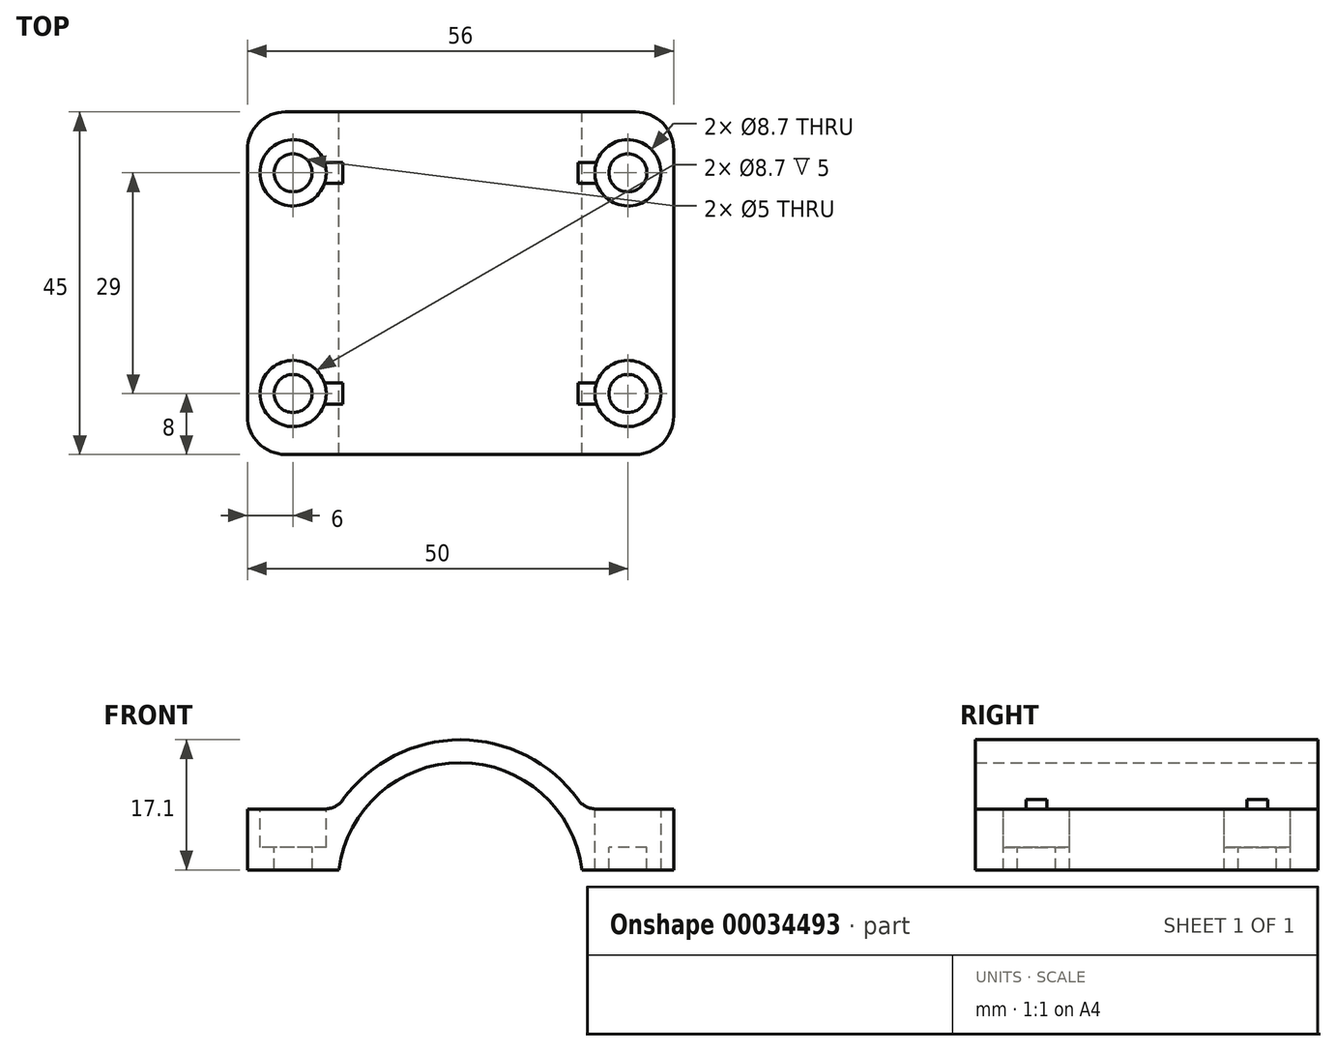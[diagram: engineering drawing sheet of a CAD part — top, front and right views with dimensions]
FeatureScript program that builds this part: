
annotation { "Feature Type Name" : "Feature", "Feature Type Description" : "" }
export const myFeature = defineFeature(function(context is Context, id is Id, definition is map)
    precondition{}
    {
        {
            var Q0;
            Q0=qCreatedBy(makeId("Front.planeOp"),FACE);
            var sketch = newSketch(context, id + "F0", { "sketchPlane" : qUnion([Q0])});
            skCircle(sketch, "E0", {"center": v(0, 0) * mm, "radius": 16.1 * mm, "construction": true});
            skLineSegment(sketch, "E1", {"start": v(-59.3, 0) * mm, "end": v(64.9, 0) * mm, "construction": true});
            skLineSegment(sketch, "E2", {"start": v(-28, 2) * mm, "end": v(-15.98, 2) * mm});
            skArc(sketch, "E3", {"start": v(15.98, 2) * mm, "mid": v(0, 16.1) * mm, "end": v(-15.98, 2) * mm});
            skArc(sketch, "E4.0", {"start": v(16.27, 10) * mm, "mid": v(0, 19.1) * mm, "end": v(-16.27, 10) * mm});
            skLineSegment(sketch, "E5", {"start": v(-28, 2) * mm, "end": v(-28, 10) * mm});
            skLineSegment(sketch, "E6", {"start": v(-28, 10) * mm, "end": v(-16.27, 10) * mm});
            skLineSegment(sketch, "E7", {"start": v(28, 10) * mm, "end": v(28, 2) * mm});
            skLineSegment(sketch, "E8.trimOffspring", {"start": v(16.27, 10) * mm, "end": v(28, 10) * mm});
            skLineSegment(sketch, "E9.trimOffspring", {"start": v(15.98, 2) * mm, "end": v(28, 2) * mm});
            skSolve(sketch);
        }
        {
            var Q0;
            Q0 = qSketchRegion(id + "F0", true);
            extrude(context, id + "F1", {"entities" : qUnion([Q0]), "depth" : 45 * mm});
        }
        {
            var Q0;
            Q0=makeQuery(id+"F1.opExtrude","SWEPT_FACE",FACE,{"disambiguationData":[OSD([sQuery(id+"F0.wireOp",EDGE,"E6")])]});
            var sketch = newSketch(context, id + "F2", { "sketchPlane" : qUnion([Q0])});
            skLineSegment(sketch, "E10", {"start": v(0, 3.28) * mm, "end": v(0, -44.43) * mm, "construction": true});
            skLineSegment(sketch, "E11", {"start": v(-22, 4.04) * mm, "end": v(-22, -45.83) * mm, "construction": true});
            skLineSegment(sketch, "E12.0", {"start": v(-28, -45) * mm, "end": v(-28, 0) * mm, "construction": true});
            skLineSegment(sketch, "E12.1", {"start": v(-28, 0) * mm, "end": v(-16.27, 0) * mm, "construction": true});
            skLineSegment(sketch, "E12.2", {"start": v(-28, -45) * mm, "end": v(-16.27, -45) * mm, "construction": true});
            skCircle(sketch, "E13", {"center": v(-22, -8) * mm, "radius": 4.35 * mm});
            skCircle(sketch, "E14", {"center": v(-22, -37) * mm, "radius": 4.35 * mm});
            skCircle(sketch, "E15", {"center": v(-22, -8) * mm, "radius": 2.5 * mm});
            skCircle(sketch, "E16", {"center": v(-22, -37) * mm, "radius": 2.5 * mm});
            skCircle(sketch, "E17.MirrorC", {"center": v(22, -8) * mm, "radius": 2.5 * mm});
            skCircle(sketch, "E18.MirrorC", {"center": v(22, -8) * mm, "radius": 4.35 * mm});
            skCircle(sketch, "E19.MirrorC", {"center": v(22, -37) * mm, "radius": 2.5 * mm});
            skCircle(sketch, "E20.MirrorC", {"center": v(22, -37) * mm, "radius": 4.35 * mm});
            skSolve(sketch);
        }
        {
            var Q0;
            Q0=makeQuery(id+"F2.imprint","IMPRINT",FACE,{"disambiguationData":[TD([[makeQuery(id+"F2.imprint","IMPRINT",EDGE,{"derivedFrom":sQuery(id+"F2.wireOp",EDGE,"E15")}),1.0]])]});
            var Q1;
            Q1=makeQuery(id+"F2.imprint","IMPRINT",FACE,{"disambiguationData":[TD([[makeQuery(id+"F2.imprint","IMPRINT",EDGE,{"derivedFrom":sQuery(id+"F2.wireOp",EDGE,"E15")}),-1.0]])]});
            var Q2;
            Q2=makeQuery(id+"F2.imprint","IMPRINT",FACE,{"disambiguationData":[TD([[makeQuery(id+"F2.imprint","IMPRINT",EDGE,{"derivedFrom":sQuery(id+"F2.wireOp",EDGE,"E17.MirrorC")}),-1.0]])]});
            var Q3;
            Q3=makeQuery(id+"F2.imprint","IMPRINT",FACE,{"disambiguationData":[TD([[makeQuery(id+"F2.imprint","IMPRINT",EDGE,{"derivedFrom":sQuery(id+"F2.wireOp",EDGE,"E17.MirrorC")}),1.0]])]});
            var Q4;
            Q4=makeQuery(id+"F2.imprint","IMPRINT",FACE,{"disambiguationData":[TD([[makeQuery(id+"F2.imprint","IMPRINT",EDGE,{"derivedFrom":sQuery(id+"F2.wireOp",EDGE,"E19.MirrorC")}),-1.0]])]});
            var Q5;
            Q5=makeQuery(id+"F2.imprint","IMPRINT",FACE,{"disambiguationData":[TD([[makeQuery(id+"F2.imprint","IMPRINT",EDGE,{"derivedFrom":sQuery(id+"F2.wireOp",EDGE,"E19.MirrorC")}),1.0]])]});
            var Q6;
            Q6=makeQuery(id+"F2.imprint","IMPRINT",FACE,{"disambiguationData":[TD([[makeQuery(id+"F2.imprint","IMPRINT",EDGE,{"derivedFrom":sQuery(id+"F2.wireOp",EDGE,"E16")}),1.0]])]});
            var Q7;
            Q7=makeQuery(id+"F2.imprint","IMPRINT",FACE,{"disambiguationData":[TD([[makeQuery(id+"F2.imprint","IMPRINT",EDGE,{"derivedFrom":sQuery(id+"F2.wireOp",EDGE,"E16")}),-1.0]])]});
            extrude(context, id + "F3", {"entities" : qUnion([Q0, Q1, Q2, Q3, Q4, Q5, Q6, Q7]), "operationType" : NewBodyOperationType.REMOVE, "oppositeDirection" : true, "depth" : 5 * mm});
        }
        {
            var Q0;
            Q0=makeQuery(id+"F2.imprint","IMPRINT",FACE,{"disambiguationData":[TD([[makeQuery(id+"F2.imprint","IMPRINT",EDGE,{"derivedFrom":sQuery(id+"F2.wireOp",EDGE,"E15")}),1.0]])]});
            var Q1;
            Q1=makeQuery(id+"F2.imprint","IMPRINT",FACE,{"disambiguationData":[TD([[makeQuery(id+"F2.imprint","IMPRINT",EDGE,{"derivedFrom":sQuery(id+"F2.wireOp",EDGE,"E17.MirrorC")}),-1.0]])]});
            var Q2;
            Q2=makeQuery(id+"F2.imprint","IMPRINT",FACE,{"disambiguationData":[TD([[makeQuery(id+"F2.imprint","IMPRINT",EDGE,{"derivedFrom":sQuery(id+"F2.wireOp",EDGE,"E16")}),1.0]])]});
            var Q3;
            Q3=makeQuery(id+"F2.imprint","IMPRINT",FACE,{"disambiguationData":[TD([[makeQuery(id+"F2.imprint","IMPRINT",EDGE,{"derivedFrom":sQuery(id+"F2.wireOp",EDGE,"E19.MirrorC")}),-1.0]])]});
            extrude(context, id + "F4", {"entities" : qUnion([Q0, Q1, Q2, Q3]), "operationType" : NewBodyOperationType.REMOVE, "endBound" : BoundingType.THROUGH_ALL, "oppositeDirection" : true, "depth" : 25 * mm});
        }
        {
            var Q0;
            Q0=makeQuery(id+"F1.opExtrude","SWEPT_EDGE",EDGE,{"disambiguationData":[OSD([sQuery(id+"F0.wireOp",EDGE,"E4.0"),sQuery(id+"F0.wireOp",EDGE,"E6")])]});
            var Q1;
            Q1=makeQuery(id+"F1.opExtrude","SWEPT_EDGE",EDGE,{"disambiguationData":[OSD([sQuery(id+"F0.wireOp",EDGE,"E4.0"),sQuery(id+"F0.wireOp",EDGE,"E8.trimOffspring")])]});
            fillet(context, id + "F5", {"entities" : qUnion([Q0, Q1]), "radius" : 3 * mm, "tangentPropagation" : true, "allowEdgeOverflow" : false});
        }
        {
            var Q0;
            Q0=makeQuery(id+"F1.opExtrude","CAP_EDGE",EDGE,{"disambiguationData":[OSD([sQuery(id+"F0.wireOp",EDGE,"E7")])],"isStart":false});
            var Q1;
            Q1=makeQuery(id+"F1.opExtrude","CAP_EDGE",EDGE,{"disambiguationData":[OSD([sQuery(id+"F0.wireOp",EDGE,"E7")])],"isStart":true});
            var Q2;
            Q2=makeQuery(id+"F1.opExtrude","CAP_EDGE",EDGE,{"disambiguationData":[OSD([sQuery(id+"F0.wireOp",EDGE,"E5")])],"isStart":false});
            var Q3;
            Q3=makeQuery(id+"F1.opExtrude","CAP_EDGE",EDGE,{"disambiguationData":[OSD([sQuery(id+"F0.wireOp",EDGE,"E5")])],"isStart":true});
            fillet(context, id + "F6", {"entities" : qUnion([Q0, Q1, Q2, Q3]), "radius" : 5 * mm, "tangentPropagation" : true, "allowEdgeOverflow" : false});
        }
    });
